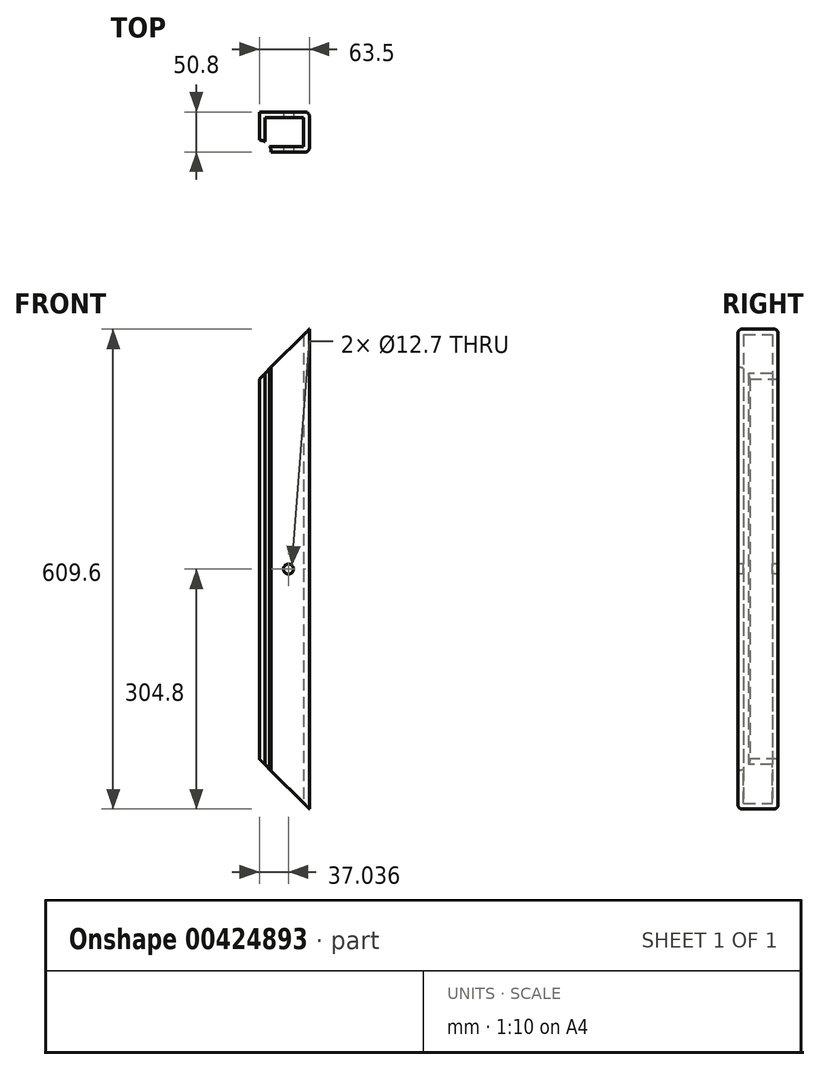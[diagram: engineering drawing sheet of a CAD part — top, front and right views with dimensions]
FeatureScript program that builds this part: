
annotation { "Feature Type Name" : "Feature", "Feature Type Description" : "" }
export const myFeature = defineFeature(function(context is Context, id is Id, definition is map)
    precondition{}
    {
        {
            var Q0;
            Q0=qCreatedBy(makeId("Top.planeOp"),FACE);
            var sketch = newSketch(context, id + "F0", { "sketchPlane" : qUnion([Q0])});
            skLineSegment(sketch, "E0.bottom", {"start": v(0, 0) * mm, "end": v(63.5, 0) * mm});
            skLineSegment(sketch, "E0.top", {"start": v(0, 50.8) * mm, "end": v(63.5, 50.8) * mm});
            skLineSegment(sketch, "E0.left", {"start": v(0, 0) * mm, "end": v(0, 50.8) * mm});
            skLineSegment(sketch, "E0.right", {"start": v(63.5, 0) * mm, "end": v(63.5, 50.8) * mm});
            skSolve(sketch);
        }
        {
            var Q0;
            Q0 = qSketchRegion(id + "F0", true);
            extrude(context, id + "F1", {"entities" : qUnion([Q0]), "depth" : 609.6 * mm});
        }
        {
            var Q0;
            Q0=makeQuery(id+"F1.opExtrude","SWEPT_FACE",FACE,{"disambiguationData":[OSD([sQuery(id+"F0.wireOp",EDGE,"E0.top")])]});
            var sketch = newSketch(context, id + "F2", { "sketchPlane" : qUnion([Q0])});
            skLineSegment(sketch, "E1", {"start": v(-63.5, 0) * mm, "end": v(13.98, 77.48) * mm});
            skLineSegment(sketch, "E2", {"start": v(-63.5, 0) * mm, "end": v(40.1, 0) * mm});
            skPoint(sketch, "E2.endSnap0", {"position": v(-31.75, 0) * mm});
            skLineSegment(sketch, "E3", {"start": v(13.98, 77.48) * mm, "end": v(40.1, 0) * mm});
            skLineSegment(sketch, "E4", {"start": v(-63.5, 304.8) * mm, "end": v(60.68, 304.8) * mm});
            skPoint(sketch, "E4.endSnap0", {"position": v(-63.5, 304.8) * mm});
            skLineSegment(sketch, "E5.MirrorCS", {"start": v(-63.5, 609.6) * mm, "end": v(13.98, 532.12) * mm});
            skLineSegment(sketch, "E6.MirrorCS", {"start": v(-63.5, 609.6) * mm, "end": v(40.1, 609.6) * mm});
            skLineSegment(sketch, "E7.MirrorCS", {"start": v(13.98, 532.12) * mm, "end": v(40.1, 609.6) * mm});
            skSolve(sketch);
        }
        {
            var Q0;
            {var subQ0=sQuery(id+"F2.wireOp",EDGE,"E3");Q0=makeQuery(id+"F2.imprint","IMPRINT",FACE,{"disambiguationData":[TD([[makeQuery(id+"F2.imprint","IMPRINT",EDGE,{"derivedFrom":subQ0}),-1.0]])]});}
            var Q1;
            {var subQ1=sQuery(id+"F2.wireOp",EDGE,"E1");var subQ2=sQuery(id+"F0.wireOp",EDGE,"E0.top");var subQ4=makeQuery(id+"F1.opExtrude","SWEPT_EDGE",EDGE,{"disambiguationData":[OSD([subQ2,sQuery(id+"F0.wireOp",EDGE,"E0.left")])]});var subQ5=makeQuery(id+"F2.imprint","INTERSECT",VERTEX,{"derivedFrom":[subQ4,subQ1]});Q1=makeQuery(id+"F2.imprint","IMPRINT",FACE,{"disambiguationData":[TD([[makeQuery(id+"F2.imprint","IMPRINT",EDGE,{"disambiguationData":[TD([[subQ5,1.0]])],"derivedFrom":subQ1}),-1.0]])]});}
            var Q2;
            {var subQ1=sQuery(id+"F2.wireOp",EDGE,"E5.MirrorCS");var subQ2=sQuery(id+"F0.wireOp",EDGE,"E0.top");var subQ4=makeQuery(id+"F1.opExtrude","SWEPT_EDGE",EDGE,{"disambiguationData":[OSD([subQ2,sQuery(id+"F0.wireOp",EDGE,"E0.left")])]});var subQ5=makeQuery(id+"F2.imprint","INTERSECT",VERTEX,{"derivedFrom":[subQ4,subQ1]});Q2=makeQuery(id+"F2.imprint","IMPRINT",FACE,{"disambiguationData":[TD([[makeQuery(id+"F2.imprint","IMPRINT",EDGE,{"disambiguationData":[TD([[subQ5,1.0]])],"derivedFrom":subQ1}),1.0]])]});}
            extrude(context, id + "F3", {"entities" : qUnion([Q0, Q1, Q2]), "operationType" : NewBodyOperationType.REMOVE, "oppositeDirection" : true, "depth" : 76.2 * mm});
        }
        {
            var Q0;
            Q0=qCreatedBy(makeId("Top.planeOp"),FACE);
            var sketch = newSketch(context, id + "F4", { "sketchPlane" : qUnion([Q0])});
            skLineSegment(sketch, "E8.0", {"start": v(7.11, 43.69) * mm, "end": v(7.11, 7.11) * mm});
            skLineSegment(sketch, "E8.1", {"start": v(56.39, 43.69) * mm, "end": v(7.11, 43.69) * mm});
            skLineSegment(sketch, "E8.2", {"start": v(56.39, 7.11) * mm, "end": v(56.39, 43.69) * mm});
            skLineSegment(sketch, "E8.3", {"start": v(56.39, 7.11) * mm, "end": v(7.11, 7.11) * mm});
            skSolve(sketch);
        }
        {
            var Q0;
            Q0=qCreatedBy(makeId("Top.planeOp"),FACE);
            var sketch = newSketch(context, id + "F5", { "sketchPlane" : qUnion([Q0])});
            skCircle(sketch, "E9", {"center": v(0, 0) * mm, "radius": 15.03 * mm});
            skSolve(sketch);
        }
        {
            var Q0;
            Q0 = qSketchRegion(id + "F5", true);
            extrude(context, id + "F6", {"entities" : qUnion([Q0]), "operationType" : NewBodyOperationType.REMOVE, "depth" : 609.6 * mm});
        }
        {
            var Q0;
            Q0=makeQuery(id+"F1.opExtrude","SWEPT_EDGE",EDGE,{"disambiguationData":[OSD([sQuery(id+"F0.wireOp",EDGE,"E0.top"),sQuery(id+"F0.wireOp",EDGE,"E0.right")])]});
            var Q1;
            Q1=makeQuery(id+"F1.opExtrude","SWEPT_EDGE",EDGE,{"disambiguationData":[OSD([sQuery(id+"F0.wireOp",EDGE,"E0.bottom"),sQuery(id+"F0.wireOp",EDGE,"E0.right")])]});
            fillet(context, id + "F7", {"entities" : qUnion([Q0, Q1]), "radius" : 5.08 * mm, "tangentPropagation" : true, "allowEdgeOverflow" : false});
        }
        {
            var Q0;
            Q0=makeQuery(id+"F1.opExtrude","SWEPT_FACE",FACE,{"disambiguationData":[OSD([sQuery(id+"F0.wireOp",EDGE,"E0.bottom")])]});
            var sketch = newSketch(context, id + "F8", { "sketchPlane" : qUnion([Q0])});
            skCircle(sketch, "E10", {"center": v(37.04, 304.8) * mm, "radius": 6.35 * mm});
            skPoint(sketch, "E10.centerSnap0", {"position": v(15.03, 304.8) * mm});
            skSolve(sketch);
        }
        {
            var Q0;
            Q0=makeQuery(id+"F8.imprint","IMPRINT",FACE,{"disambiguationData":[TD([[makeQuery(id+"F8.imprint","IMPRINT",EDGE,{"derivedFrom":sQuery(id+"F8.wireOp",EDGE,"E10")}),1.0]])]});
            extrude(context, id + "F9", {"entities" : qUnion([Q0]), "operationType" : NewBodyOperationType.REMOVE, "oppositeDirection" : true, "depth" : 76.2 * mm});
        }
        {
            var Q0;
            Q0=makeQuery(id+"F4.imprint","IMPRINT",FACE,{"disambiguationData":[TD([[makeQuery(id+"F4.imprint","IMPRINT",EDGE,{"derivedFrom":sQuery(id+"F4.wireOp",EDGE,"E8.0")}),1.0]])]});
            extrude(context, id + "F10", {"entities" : qUnion([Q0]), "operationType" : NewBodyOperationType.REMOVE, "depth" : 609.6 * mm});
        }
    });
